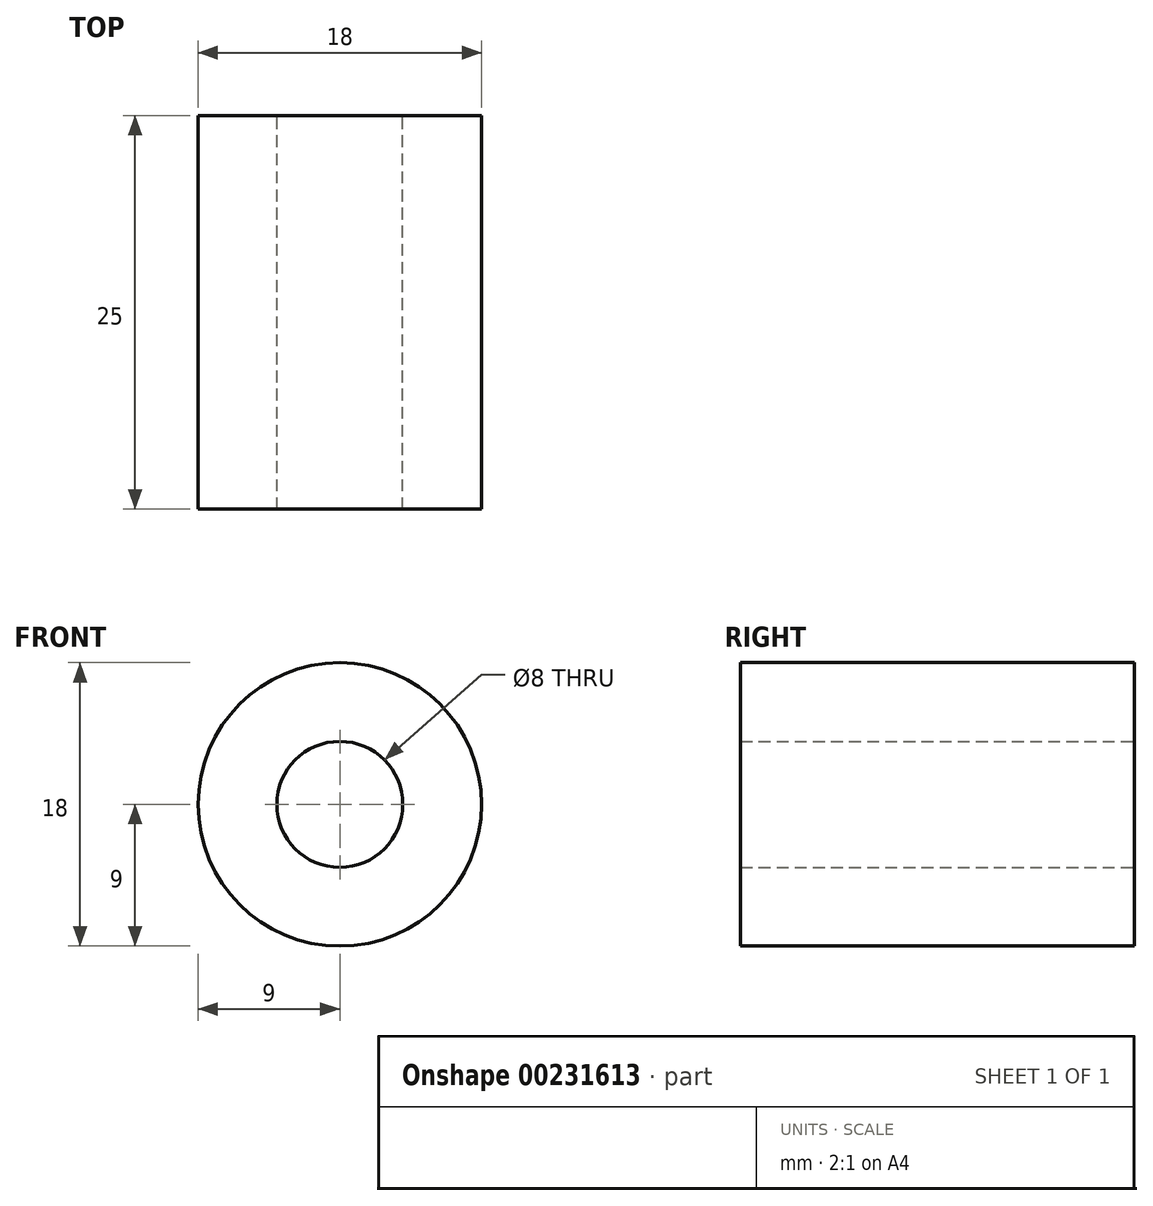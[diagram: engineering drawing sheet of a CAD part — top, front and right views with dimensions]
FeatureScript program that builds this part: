
annotation { "Feature Type Name" : "Feature", "Feature Type Description" : "" }
export const myFeature = defineFeature(function(context is Context, id is Id, definition is map)
    precondition{}
    {
        {
            var Q0;
            Q0=qCreatedBy(makeId("Front.planeOp"),FACE);
            var sketch = newSketch(context, id + "F0", { "sketchPlane" : qUnion([Q0])});
            skCircle(sketch, "E0", {"center": v(0, 0) * mm, "radius": 9 * mm});
            skCircle(sketch, "E1", {"center": v(0, 0) * mm, "radius": 4 * mm});
            skSolve(sketch);
        }
        {
            var Q0;
            Q0 = qSketchRegion(id + "F0", true);
            extrude(context, id + "F1", {"entities" : qUnion([Q0]), "depth" : 25 * mm});
        }
    });
